# Revit family: KDW010098
name_source: partatom
category: Appareils sanitaires
revit_build: Autodesk Revit Architecture 2015 (Build: 20140223_1515(x64)
units: mm (PartAtom-declared; Revit-internal decimal feet)

## types (1)
- CONO WANDWASCHTISCH 3089 500x600
    Color = https://www.kaldewei.co.uk
    ColourOptions = https://www.kaldewei.co.uk
    Durability = https://www.kaldewei.de
    Fabricant = Kaldewei
    Features = https://www.kaldewei.co.uk
    Finish = https://n
    Finition = Kaldewei
    HasGrabHandles = https://www.kaldewei.co.uk
    IfcExportAs = WASHHANDBASIN
    IfcExportType = IfcSanitaryTerminalType
    IntegralAccessories = https://www.kaldewei.co.uk
    ManufacturerCountry = GERMANY
    ManufacturerName = KALDEWEI
    ManufacturerURL = https://www.kaldewei.com
    Material = steel enamel
    Metal = Acier, chromé
    Modèle = CONOWANDWASCHTISCH
    Name = CONOWANDWASCHTISCH
    NominalHeight = 120 mm
    NominalLength = 600
    NominalWidth = 500
    ObjectName = CONO all-hung washbasin 500x600
    ObjectNorm = EN 14688EU DECLARATION OF PERFORMANCE(https://www.kaldewei.de
    ObjectPicture = https://www.kaldewei.co.uk
    ObjectURL = https://www.kaldewei.co.uk
    Polantis code = KDW010098
    ProductInformation = Model No.3089: - washbasin with premium character exudes elegance and harmony- optimally integrated enamelled waste accentuates the underlying geometry of the washbasin- unusually generous rim provides space for fittings or individual accessories- perfectly complements the Cono range- All CONO washbasins of 120 cm width are available now with 1x1 or 1x3 tap holes
    Revision = 1
    SerialNumber = 3089
    Shape = Wall-Hung,Double washbasin
    Size = 500x600
    SupportFrame = https://www.kaldewei.co.uk
    Sustainability = https://kaldewei-fa.secure.footprint.net
    TechnicalDataURL = https://kaldewei.typo-live.web-factory.de
    Type Comments = CONO WANDWASCHTISCH 3089 500x600
    UNSPSCCode = 30181504
    UNSPSCNames = Sinks
    URL = https://www.kaldewei.co.uk
    Uniclass 2015 = Pr_40_20_96
    Version = 4
    WarrantyDurationParts = 30
    WarrantyDurationUnit = Year
    WarrantyStartDate = https://www.kaldewei.co.uk
    Weight = 15

## geometry (parser evidence)
native form markers: Sweep x3
no freeform markers — native parametric forms only
